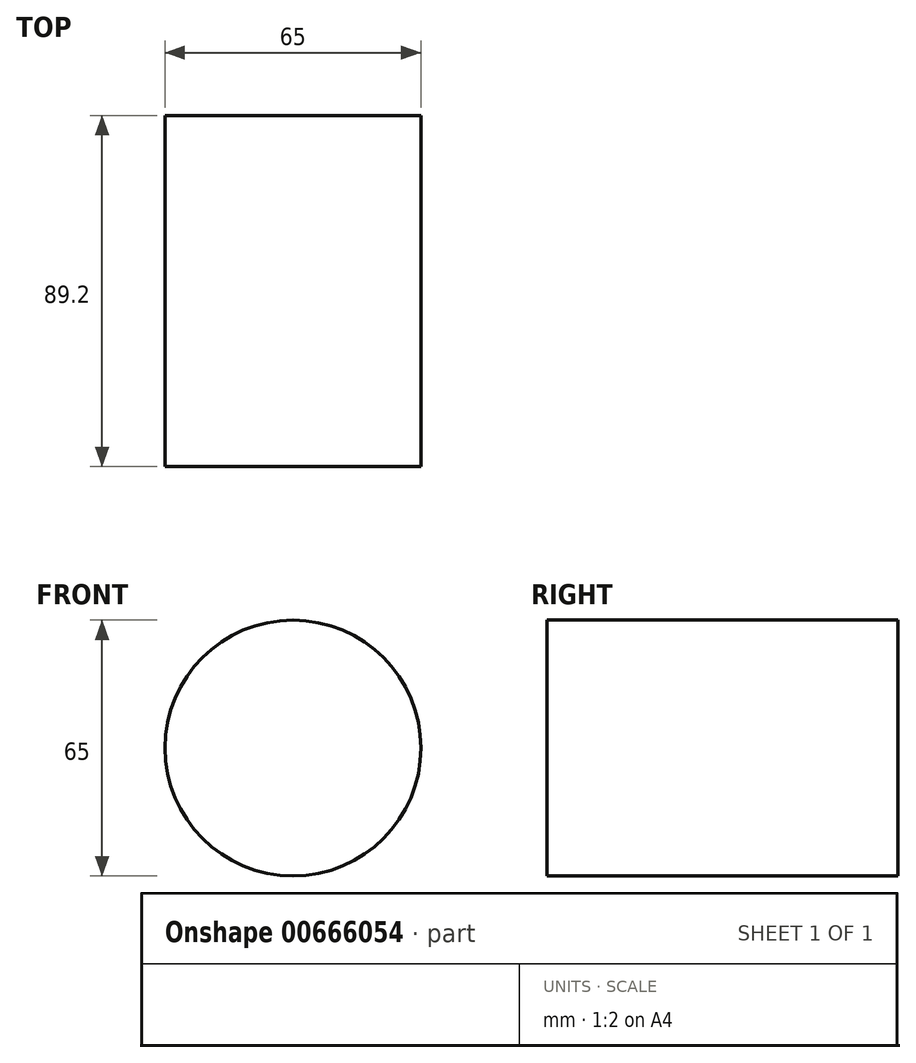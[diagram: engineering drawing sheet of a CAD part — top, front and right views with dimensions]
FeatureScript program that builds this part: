
annotation { "Feature Type Name" : "Feature", "Feature Type Description" : "" }
export const myFeature = defineFeature(function(context is Context, id is Id, definition is map)
    precondition{}
    {
        {
            var Q0;
            Q0=qCreatedBy(makeId("Front.planeOp"),FACE);
            var sketch = newSketch(context, id + "F0", { "sketchPlane" : qUnion([Q0])});
            skCircle(sketch, "E0", {"center": v(0, 0) * mm, "radius": 32.5 * mm});
            skSolve(sketch);
        }
        {
            var Q0;
            Q0=makeQuery(id+"F0.imprint","IMPRINT",FACE,{"disambiguationData":[TD([[makeQuery(id+"F0.imprint","IMPRINT",EDGE,{"derivedFrom":sQuery(id+"F0.wireOp",EDGE,"E0")}),1.0]])]});
            extrude(context, id + "F1", {"entities" : qUnion([Q0]), "endBound" : BoundingType.SYMMETRIC, "depth" : 89.2 * mm, "offsetDistance" : 25 * mm});
        }
        {
            var Q0;
            Q0=qCreatedBy(makeId("Right.planeOp"),FACE);
            cPlane(context, id + "F2", {"entities" : qUnion([Q0]), "cplaneType" : CPlaneType.OFFSET, "offset" : 94.5 * mm, "width" : 150 * mm, "height" : 150 * mm});
        }
    });
